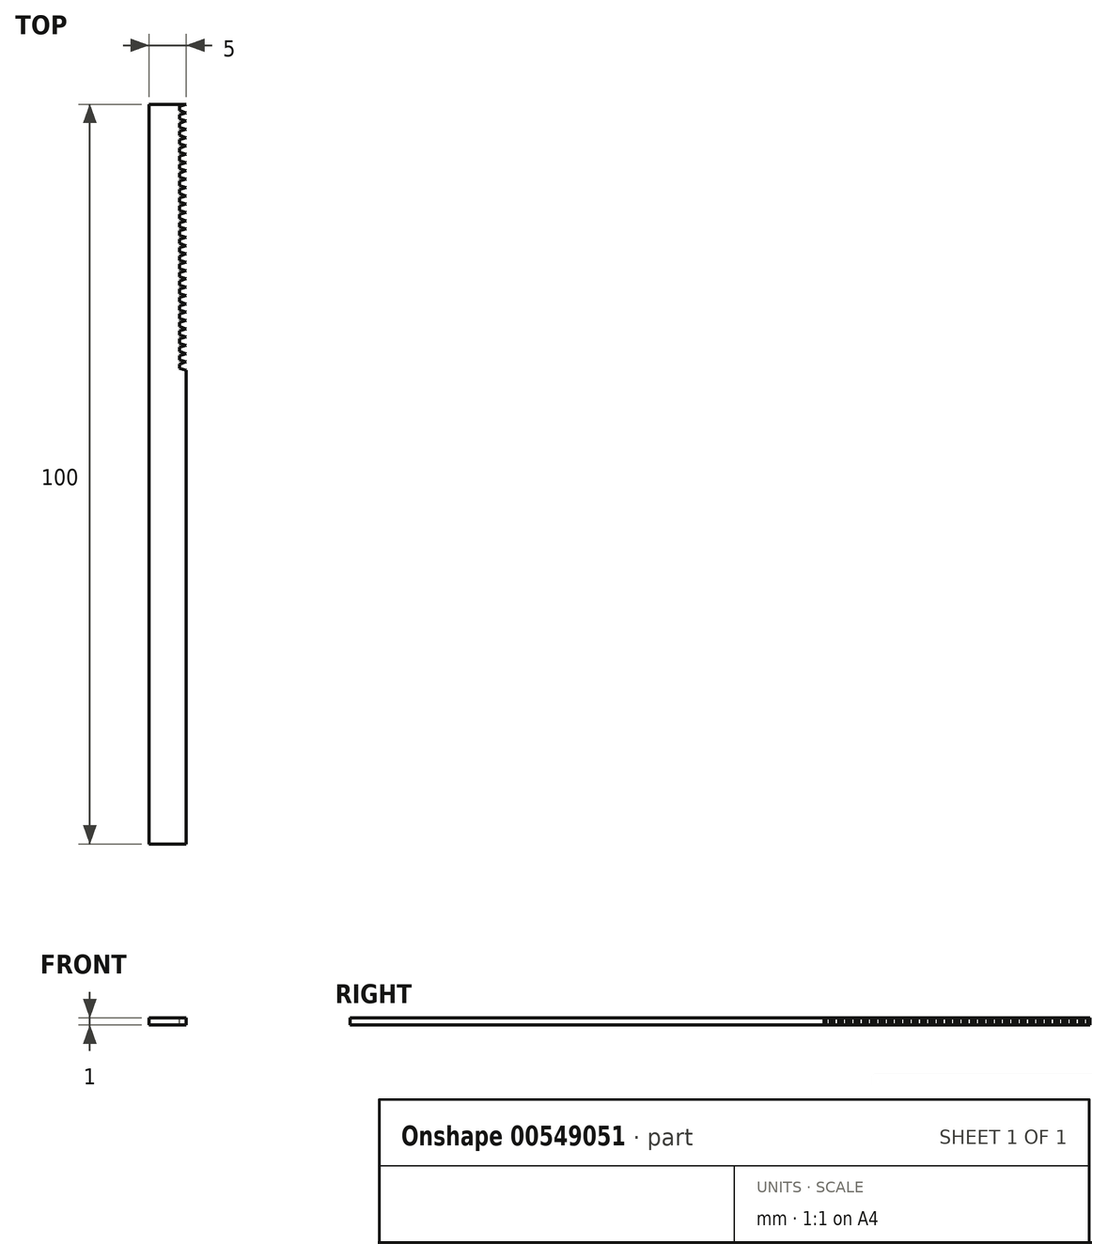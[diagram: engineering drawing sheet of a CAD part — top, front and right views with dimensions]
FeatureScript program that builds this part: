
annotation { "Feature Type Name" : "Feature", "Feature Type Description" : "" }
export const myFeature = defineFeature(function(context is Context, id is Id, definition is map)
    precondition{}
    {
        {
            var Q0;
            Q0=qCreatedBy(makeId("Top.planeOp"),FACE);
            var sketch = newSketch(context, id + "F0", { "sketchPlane" : qUnion([Q0])});
            skLineSegment(sketch, "E0.bottom", {"start": v(-60.96, 22.46) * mm, "end": v(-55.96, 22.46) * mm});
            skLineSegment(sketch, "E0.top", {"start": v(-60.96, -77.54) * mm, "end": v(-55.96, -77.54) * mm});
            skLineSegment(sketch, "E0.left", {"start": v(-60.96, 22.46) * mm, "end": v(-60.96, -77.54) * mm});
            skLineSegment(sketch, "E0.right", {"start": v(-55.96, 22.46) * mm, "end": v(-55.96, -77.54) * mm});
            skSolve(sketch);
        }
        {
            var Q0;
            Q0 = qSketchRegion(id + "F0", true);
            extrude(context, id + "F1", {"entities" : qUnion([Q0]), "endBound" : BoundingType.SYMMETRIC, "depth" : 1 * mm, "offsetDistance" : 25 * mm});
        }
        {
            var Q0;
            Q0=makeQuery(id+"F1.opExtrude","CAP_FACE",FACE,{"disambiguationData":[OSD([sQuery(id+"F0.wireOp",EDGE,"E0.bottom"),sQuery(id+"F0.wireOp",EDGE,"E0.top"),sQuery(id+"F0.wireOp",EDGE,"E0.left"),sQuery(id+"F0.wireOp",EDGE,"E0.right")])],"isStart":false});
            var sketch = newSketch(context, id + "F2", { "sketchPlane" : qUnion([Q0])});
            skLineSegment(sketch, "E1", {"start": v(-56.84, 22.18) * mm, "end": v(-56.84, 21.6) * mm});
            skLineSegment(sketch, "E2", {"start": v(-56.84, 21.6) * mm, "end": v(-55.96, 21.32) * mm});
            skLineSegment(sketch, "E3", {"start": v(-56.84, 22.18) * mm, "end": v(-55.96, 22.45) * mm});
            skLineSegment(sketch, "E4.MirrorCS", {"start": v(-56.84, 21.06) * mm, "end": v(-55.96, 21.32) * mm});
            skLineSegment(sketch, "E5.MirrorCS", {"start": v(-56.84, 20.47) * mm, "end": v(-56.84, 21.06) * mm});
            skLineSegment(sketch, "E6.MirrorCS", {"start": v(-56.84, 20.47) * mm, "end": v(-55.96, 20.2) * mm});
            skLineSegment(sketch, "E7.MirrorCS", {"start": v(-56.84, 19.93) * mm, "end": v(-55.96, 20.2) * mm});
            skLineSegment(sketch, "E8.MirrorCS", {"start": v(-56.84, 19.93) * mm, "end": v(-56.84, 19.34) * mm});
            skLineSegment(sketch, "E9.MirrorCS", {"start": v(-56.84, 19.34) * mm, "end": v(-55.96, 19.08) * mm});
            skLineSegment(sketch, "E10.MirrorCS", {"start": v(-56.84, 18.81) * mm, "end": v(-55.96, 19.08) * mm});
            skLineSegment(sketch, "E11.MirrorCS", {"start": v(-56.84, 18.22) * mm, "end": v(-56.84, 18.81) * mm});
            skLineSegment(sketch, "E12.MirrorCS", {"start": v(-56.84, 18.22) * mm, "end": v(-55.96, 17.95) * mm});
            skLineSegment(sketch, "E13.MirrorCS", {"start": v(-56.84, 14.85) * mm, "end": v(-55.96, 14.58) * mm});
            skLineSegment(sketch, "E14.MirrorCS", {"start": v(-56.84, 13.73) * mm, "end": v(-55.96, 13.46) * mm});
            skLineSegment(sketch, "E15.MirrorCS", {"start": v(-56.84, 15.97) * mm, "end": v(-55.96, 15.7) * mm});
            skLineSegment(sketch, "E16.MirrorCS", {"start": v(-56.84, 14.32) * mm, "end": v(-55.96, 14.58) * mm});
            skLineSegment(sketch, "E17.MirrorCS", {"start": v(-56.84, 13.73) * mm, "end": v(-56.84, 14.32) * mm});
            skLineSegment(sketch, "E18.MirrorCS", {"start": v(-56.84, 17.1) * mm, "end": v(-55.96, 16.83) * mm});
            skLineSegment(sketch, "E19.MirrorCS", {"start": v(-56.84, 15.97) * mm, "end": v(-56.84, 16.56) * mm});
            skLineSegment(sketch, "E20.MirrorCS", {"start": v(-56.84, 15.44) * mm, "end": v(-55.96, 15.7) * mm});
            skLineSegment(sketch, "E21.MirrorCS", {"start": v(-56.84, 17.69) * mm, "end": v(-55.96, 17.95) * mm});
            skLineSegment(sketch, "E22.MirrorCS", {"start": v(-56.84, 16.56) * mm, "end": v(-55.96, 16.83) * mm});
            skLineSegment(sketch, "E23.MirrorCS", {"start": v(-56.84, 15.44) * mm, "end": v(-56.84, 14.85) * mm});
            skLineSegment(sketch, "E24.MirrorCS", {"start": v(-56.84, 17.69) * mm, "end": v(-56.84, 17.1) * mm});
            skLineSegment(sketch, "E25.MirrorCS", {"start": v(-56.84, 9.23) * mm, "end": v(-56.84, 9.82) * mm});
            skLineSegment(sketch, "E26.MirrorCS", {"start": v(-56.84, 5.86) * mm, "end": v(-55.96, 5.6) * mm});
            skLineSegment(sketch, "E27.MirrorCS", {"start": v(-56.84, 4.74) * mm, "end": v(-55.96, 4.47) * mm});
            skLineSegment(sketch, "E28.MirrorCS", {"start": v(-56.84, 5.33) * mm, "end": v(-55.96, 5.6) * mm});
            skLineSegment(sketch, "E29.MirrorCS", {"start": v(-56.84, 4.74) * mm, "end": v(-56.84, 5.33) * mm});
            skLineSegment(sketch, "E30.MirrorCS", {"start": v(-56.84, 12.6) * mm, "end": v(-55.96, 12.34) * mm});
            skLineSegment(sketch, "E31.MirrorCS", {"start": v(-56.84, 10.95) * mm, "end": v(-55.96, 11.21) * mm});
            skLineSegment(sketch, "E32.MirrorCS", {"start": v(-56.84, 13.2) * mm, "end": v(-55.96, 13.46) * mm});
            skLineSegment(sketch, "E33.MirrorCS", {"start": v(-56.84, 11.48) * mm, "end": v(-55.96, 11.21) * mm});
            skLineSegment(sketch, "E34.MirrorCS", {"start": v(-56.84, 9.82) * mm, "end": v(-55.96, 10.1) * mm});
            skLineSegment(sketch, "E35.MirrorCS", {"start": v(-56.84, 10.36) * mm, "end": v(-55.96, 10.1) * mm});
            skLineSegment(sketch, "E36.MirrorCS", {"start": v(-56.84, 6.45) * mm, "end": v(-55.96, 6.72) * mm});
            skLineSegment(sketch, "E37.MirrorCS", {"start": v(-56.84, 7.58) * mm, "end": v(-55.96, 7.84) * mm});
            skLineSegment(sketch, "E38.MirrorCS", {"start": v(-56.84, 6.99) * mm, "end": v(-55.96, 6.72) * mm});
            skLineSegment(sketch, "E39.MirrorCS", {"start": v(-56.84, 8.11) * mm, "end": v(-55.96, 7.84) * mm});
            skLineSegment(sketch, "E40.MirrorCS", {"start": v(-56.84, 10.95) * mm, "end": v(-56.84, 10.36) * mm});
            skLineSegment(sketch, "E41.MirrorCS", {"start": v(-56.84, 12.07) * mm, "end": v(-55.96, 12.34) * mm});
            skLineSegment(sketch, "E42.MirrorCS", {"start": v(-56.84, 8.7) * mm, "end": v(-56.84, 8.11) * mm});
            skLineSegment(sketch, "E43.MirrorCS", {"start": v(-56.84, 8.7) * mm, "end": v(-55.96, 8.97) * mm});
            skLineSegment(sketch, "E44.MirrorCS", {"start": v(-56.84, 6.99) * mm, "end": v(-56.84, 7.58) * mm});
            skLineSegment(sketch, "E45.MirrorCS", {"start": v(-56.84, 9.23) * mm, "end": v(-55.96, 8.97) * mm});
            skLineSegment(sketch, "E46.MirrorCS", {"start": v(-56.84, 6.45) * mm, "end": v(-56.84, 5.86) * mm});
            skLineSegment(sketch, "E47.MirrorCS", {"start": v(-56.84, 11.48) * mm, "end": v(-56.84, 12.07) * mm});
            skLineSegment(sketch, "E48.MirrorCS", {"start": v(-56.84, 13.2) * mm, "end": v(-56.84, 12.6) * mm});
            skLineSegment(sketch, "E49.MirrorCS", {"start": v(-56.84, -11.52) * mm, "end": v(-56.84, -12.1) * mm});
            skLineSegment(sketch, "E50.MirrorCS", {"start": v(-56.84, -9.86) * mm, "end": v(-55.96, -10.13) * mm});
            skLineSegment(sketch, "E51.MirrorCS", {"start": v(-56.84, -10.4) * mm, "end": v(-55.96, -10.13) * mm});
            skLineSegment(sketch, "E52.MirrorCS", {"start": v(-56.84, -10.99) * mm, "end": v(-56.84, -10.4) * mm});
            skLineSegment(sketch, "E53.MirrorCS", {"start": v(-56.84, -11.52) * mm, "end": v(-55.96, -11.25) * mm});
            skLineSegment(sketch, "E54.MirrorCS", {"start": v(-56.84, -10.99) * mm, "end": v(-55.96, -11.25) * mm});
            skLineSegment(sketch, "E55.MirrorCS", {"start": v(-56.84, -12.1) * mm, "end": v(-55.96, -12.38) * mm});
            skLineSegment(sketch, "E56.MirrorCS", {"start": v(-56.84, -13.23) * mm, "end": v(-55.96, -13.5) * mm});
            skLineSegment(sketch, "E57.MirrorCS", {"start": v(-56.84, 2.5) * mm, "end": v(-55.96, 2.23) * mm});
            skLineSegment(sketch, "E58.MirrorCS", {"start": v(-56.84, -6.5) * mm, "end": v(-55.96, -6.76) * mm});
            skLineSegment(sketch, "E59.MirrorCS", {"start": v(-56.84, -9.27) * mm, "end": v(-56.84, -9.86) * mm});
            skLineSegment(sketch, "E60.MirrorCS", {"start": v(-56.84, -12.64) * mm, "end": v(-55.96, -12.38) * mm});
            skLineSegment(sketch, "E61.MirrorCS", {"start": v(-56.84, 4.2) * mm, "end": v(-55.96, 4.47) * mm});
            skLineSegment(sketch, "E62.MirrorCS", {"start": v(-56.84, 0.25) * mm, "end": v(-55.96, -0.02) * mm});
            skLineSegment(sketch, "E63.MirrorCS", {"start": v(-56.84, -13.23) * mm, "end": v(-56.84, -12.64) * mm});
            skLineSegment(sketch, "E64.MirrorCS", {"start": v(-56.84, -5.37) * mm, "end": v(-55.96, -5.64) * mm});
            skLineSegment(sketch, "E65.MirrorCS", {"start": v(-56.84, -0.29) * mm, "end": v(-55.96, -0.02) * mm});
            skLineSegment(sketch, "E66.MirrorCS", {"start": v(-56.84, 4.2) * mm, "end": v(-56.84, 3.62) * mm});
            skLineSegment(sketch, "E67.MirrorCS", {"start": v(-56.84, -3.12) * mm, "end": v(-55.96, -3.39) * mm});
            skLineSegment(sketch, "E68.MirrorCS", {"start": v(-56.84, -0.29) * mm, "end": v(-56.84, -0.88) * mm});
            skLineSegment(sketch, "E69.MirrorCS", {"start": v(-56.84, 1.96) * mm, "end": v(-55.96, 2.23) * mm});
            skLineSegment(sketch, "E70.MirrorCS", {"start": v(-56.84, -2) * mm, "end": v(-55.96, -2.27) * mm});
            skLineSegment(sketch, "E71.MirrorCS", {"start": v(-56.84, -7.62) * mm, "end": v(-55.96, -7.88) * mm});
            skLineSegment(sketch, "E72.MirrorCS", {"start": v(-56.84, -7.03) * mm, "end": v(-56.84, -7.62) * mm});
            skLineSegment(sketch, "E73.MirrorCS", {"start": v(-56.84, -2.53) * mm, "end": v(-56.84, -3.12) * mm});
            skLineSegment(sketch, "E74.MirrorCS", {"start": v(-56.84, -0.88) * mm, "end": v(-55.96, -1.14) * mm});
            skLineSegment(sketch, "E75.MirrorCS", {"start": v(-56.84, -8.15) * mm, "end": v(-55.96, -7.88) * mm});
            skLineSegment(sketch, "E76.MirrorCS", {"start": v(-56.84, 1.96) * mm, "end": v(-56.84, 1.37) * mm});
            skLineSegment(sketch, "E77.MirrorCS", {"start": v(-56.84, 3.62) * mm, "end": v(-55.96, 3.35) * mm});
            skLineSegment(sketch, "E78.MirrorCS", {"start": v(-56.84, -2) * mm, "end": v(-56.84, -1.4) * mm});
            skLineSegment(sketch, "E79.MirrorCS", {"start": v(-56.84, -4.78) * mm, "end": v(-56.84, -5.37) * mm});
            skLineSegment(sketch, "E80.MirrorCS", {"start": v(-56.84, -2.53) * mm, "end": v(-55.96, -2.27) * mm});
            skLineSegment(sketch, "E81.MirrorCS", {"start": v(-56.84, -8.74) * mm, "end": v(-56.84, -8.15) * mm});
            skLineSegment(sketch, "E82.MirrorCS", {"start": v(-56.84, -1.4) * mm, "end": v(-55.96, -1.14) * mm});
            skLineSegment(sketch, "E83.MirrorCS", {"start": v(-56.84, -3.66) * mm, "end": v(-55.96, -3.39) * mm});
            skLineSegment(sketch, "E84.MirrorCS", {"start": v(-56.84, -7.03) * mm, "end": v(-55.96, -6.76) * mm});
            skLineSegment(sketch, "E85.MirrorCS", {"start": v(-56.84, -4.25) * mm, "end": v(-56.84, -3.66) * mm});
            skLineSegment(sketch, "E86.MirrorCS", {"start": v(-56.84, 2.5) * mm, "end": v(-56.84, 3.08) * mm});
            skLineSegment(sketch, "E87.MirrorCS", {"start": v(-56.84, -6.5) * mm, "end": v(-56.84, -5.9) * mm});
            skLineSegment(sketch, "E88.MirrorCS", {"start": v(-56.84, -4.25) * mm, "end": v(-55.96, -4.51) * mm});
            skLineSegment(sketch, "E89.MirrorCS", {"start": v(-56.84, 0.84) * mm, "end": v(-55.96, 1.1) * mm});
            skLineSegment(sketch, "E90.MirrorCS", {"start": v(-56.84, -8.74) * mm, "end": v(-55.96, -9) * mm});
            skLineSegment(sketch, "E91.MirrorCS", {"start": v(-56.84, -5.9) * mm, "end": v(-55.96, -5.64) * mm});
            skLineSegment(sketch, "E92.MirrorCS", {"start": v(-56.84, -4.78) * mm, "end": v(-55.96, -4.51) * mm});
            skLineSegment(sketch, "E93.MirrorCS", {"start": v(-56.84, 3.08) * mm, "end": v(-55.96, 3.35) * mm});
            skLineSegment(sketch, "E94.MirrorCS", {"start": v(-56.84, 0.25) * mm, "end": v(-56.84, 0.84) * mm});
            skLineSegment(sketch, "E95.MirrorCS", {"start": v(-56.84, -9.27) * mm, "end": v(-55.96, -9) * mm});
            skLineSegment(sketch, "E96.MirrorCS", {"start": v(-56.84, 1.37) * mm, "end": v(-55.96, 1.1) * mm});
            skSolve(sketch);
        }
        {
            var Q0;
            Q0=makeQuery(id+"F2.imprint","IMPRINT",FACE,{"disambiguationData":[TD([[makeQuery(id+"F2.imprint","IMPRINT",EDGE,{"derivedFrom":sQuery(id+"F2.wireOp",EDGE,"E1")}),1.0]])]});
            var Q1;
            {var subQ0=sQuery(id+"F2.wireOp",EDGE,"E4.MirrorCS");Q1=makeQuery(id+"F2.imprint","IMPRINT",FACE,{"disambiguationData":[TD([[makeQuery(id+"F2.imprint","IMPRINT",EDGE,{"derivedFrom":subQ0}),-1.0]])]});}
            var Q2;
            {var subQ0=sQuery(id+"F2.wireOp",EDGE,"E7.MirrorCS");Q2=makeQuery(id+"F2.imprint","IMPRINT",FACE,{"disambiguationData":[TD([[makeQuery(id+"F2.imprint","IMPRINT",EDGE,{"derivedFrom":subQ0}),-1.0]])]});}
            var Q3;
            {var subQ0=sQuery(id+"F2.wireOp",EDGE,"E10.MirrorCS");Q3=makeQuery(id+"F2.imprint","IMPRINT",FACE,{"disambiguationData":[TD([[makeQuery(id+"F2.imprint","IMPRINT",EDGE,{"derivedFrom":subQ0}),-1.0]])]});}
            var Q4;
            {var subQ0=sQuery(id+"F2.wireOp",EDGE,"E18.MirrorCS");Q4=makeQuery(id+"F2.imprint","IMPRINT",FACE,{"disambiguationData":[TD([[makeQuery(id+"F2.imprint","IMPRINT",EDGE,{"derivedFrom":subQ0}),1.0]])]});}
            var Q5;
            {var subQ0=sQuery(id+"F2.wireOp",EDGE,"E15.MirrorCS");Q5=makeQuery(id+"F2.imprint","IMPRINT",FACE,{"disambiguationData":[TD([[makeQuery(id+"F2.imprint","IMPRINT",EDGE,{"derivedFrom":subQ0}),1.0]])]});}
            var Q6;
            {var subQ0=sQuery(id+"F2.wireOp",EDGE,"E13.MirrorCS");Q6=makeQuery(id+"F2.imprint","IMPRINT",FACE,{"disambiguationData":[TD([[makeQuery(id+"F2.imprint","IMPRINT",EDGE,{"derivedFrom":subQ0}),1.0]])]});}
            var Q7;
            {var subQ0=sQuery(id+"F2.wireOp",EDGE,"E14.MirrorCS");Q7=makeQuery(id+"F2.imprint","IMPRINT",FACE,{"disambiguationData":[TD([[makeQuery(id+"F2.imprint","IMPRINT",EDGE,{"derivedFrom":subQ0}),1.0]])]});}
            var Q8;
            {var subQ0=sQuery(id+"F2.wireOp",EDGE,"E30.MirrorCS");Q8=makeQuery(id+"F2.imprint","IMPRINT",FACE,{"disambiguationData":[TD([[makeQuery(id+"F2.imprint","IMPRINT",EDGE,{"derivedFrom":subQ0}),1.0]])]});}
            var Q9;
            {var subQ0=sQuery(id+"F2.wireOp",EDGE,"E33.MirrorCS");Q9=makeQuery(id+"F2.imprint","IMPRINT",FACE,{"disambiguationData":[TD([[makeQuery(id+"F2.imprint","IMPRINT",EDGE,{"derivedFrom":subQ0}),1.0]])]});}
            var Q10;
            {var subQ0=sQuery(id+"F2.wireOp",EDGE,"E31.MirrorCS");Q10=makeQuery(id+"F2.imprint","IMPRINT",FACE,{"disambiguationData":[TD([[makeQuery(id+"F2.imprint","IMPRINT",EDGE,{"derivedFrom":subQ0}),-1.0]])]});}
            var Q11;
            Q11=makeQuery(id+"F2.imprint","IMPRINT",FACE,{"disambiguationData":[TD([[makeQuery(id+"F2.imprint","IMPRINT",EDGE,{"derivedFrom":sQuery(id+"F2.wireOp",EDGE,"E25.MirrorCS")}),-1.0]])]});
            var Q12;
            {var subQ0=sQuery(id+"F2.wireOp",EDGE,"E39.MirrorCS");Q12=makeQuery(id+"F2.imprint","IMPRINT",FACE,{"disambiguationData":[TD([[makeQuery(id+"F2.imprint","IMPRINT",EDGE,{"derivedFrom":subQ0}),1.0]])]});}
            var Q13;
            {var subQ0=sQuery(id+"F2.wireOp",EDGE,"E37.MirrorCS");Q13=makeQuery(id+"F2.imprint","IMPRINT",FACE,{"disambiguationData":[TD([[makeQuery(id+"F2.imprint","IMPRINT",EDGE,{"derivedFrom":subQ0}),-1.0]])]});}
            var Q14;
            {var subQ0=sQuery(id+"F2.wireOp",EDGE,"E26.MirrorCS");Q14=makeQuery(id+"F2.imprint","IMPRINT",FACE,{"disambiguationData":[TD([[makeQuery(id+"F2.imprint","IMPRINT",EDGE,{"derivedFrom":subQ0}),1.0]])]});}
            var Q15;
            {var subQ0=sQuery(id+"F2.wireOp",EDGE,"E27.MirrorCS");Q15=makeQuery(id+"F2.imprint","IMPRINT",FACE,{"disambiguationData":[TD([[makeQuery(id+"F2.imprint","IMPRINT",EDGE,{"derivedFrom":subQ0}),1.0]])]});}
            var Q16;
            {var subQ0=sQuery(id+"F2.wireOp",EDGE,"E61.MirrorCS");Q16=makeQuery(id+"F2.imprint","IMPRINT",FACE,{"disambiguationData":[TD([[makeQuery(id+"F2.imprint","IMPRINT",EDGE,{"derivedFrom":subQ0}),-1.0]])]});}
            var Q17;
            {var subQ0=sQuery(id+"F2.wireOp",EDGE,"E57.MirrorCS");Q17=makeQuery(id+"F2.imprint","IMPRINT",FACE,{"disambiguationData":[TD([[makeQuery(id+"F2.imprint","IMPRINT",EDGE,{"derivedFrom":subQ0}),1.0]])]});}
            var Q18;
            {var subQ0=sQuery(id+"F2.wireOp",EDGE,"E69.MirrorCS");Q18=makeQuery(id+"F2.imprint","IMPRINT",FACE,{"disambiguationData":[TD([[makeQuery(id+"F2.imprint","IMPRINT",EDGE,{"derivedFrom":subQ0}),-1.0]])]});}
            var Q19;
            {var subQ0=sQuery(id+"F2.wireOp",EDGE,"E62.MirrorCS");Q19=makeQuery(id+"F2.imprint","IMPRINT",FACE,{"disambiguationData":[TD([[makeQuery(id+"F2.imprint","IMPRINT",EDGE,{"derivedFrom":subQ0}),1.0]])]});}
            var Q20;
            {var subQ0=sQuery(id+"F2.wireOp",EDGE,"E65.MirrorCS");Q20=makeQuery(id+"F2.imprint","IMPRINT",FACE,{"disambiguationData":[TD([[makeQuery(id+"F2.imprint","IMPRINT",EDGE,{"derivedFrom":subQ0}),-1.0]])]});}
            var Q21;
            {var subQ0=sQuery(id+"F2.wireOp",EDGE,"E70.MirrorCS");Q21=makeQuery(id+"F2.imprint","IMPRINT",FACE,{"disambiguationData":[TD([[makeQuery(id+"F2.imprint","IMPRINT",EDGE,{"derivedFrom":subQ0}),1.0]])]});}
            var Q22;
            {var subQ0=sQuery(id+"F2.wireOp",EDGE,"E67.MirrorCS");Q22=makeQuery(id+"F2.imprint","IMPRINT",FACE,{"disambiguationData":[TD([[makeQuery(id+"F2.imprint","IMPRINT",EDGE,{"derivedFrom":subQ0}),1.0]])]});}
            var Q23;
            {var subQ0=sQuery(id+"F2.wireOp",EDGE,"E83.MirrorCS");Q23=makeQuery(id+"F2.imprint","IMPRINT",FACE,{"disambiguationData":[TD([[makeQuery(id+"F2.imprint","IMPRINT",EDGE,{"derivedFrom":subQ0}),-1.0]])]});}
            var Q24;
            {var subQ0=sQuery(id+"F2.wireOp",EDGE,"E64.MirrorCS");Q24=makeQuery(id+"F2.imprint","IMPRINT",FACE,{"disambiguationData":[TD([[makeQuery(id+"F2.imprint","IMPRINT",EDGE,{"derivedFrom":subQ0}),1.0]])]});}
            var Q25;
            {var subQ0=sQuery(id+"F2.wireOp",EDGE,"E58.MirrorCS");Q25=makeQuery(id+"F2.imprint","IMPRINT",FACE,{"disambiguationData":[TD([[makeQuery(id+"F2.imprint","IMPRINT",EDGE,{"derivedFrom":subQ0}),1.0]])]});}
            var Q26;
            {var subQ0=sQuery(id+"F2.wireOp",EDGE,"E71.MirrorCS");Q26=makeQuery(id+"F2.imprint","IMPRINT",FACE,{"disambiguationData":[TD([[makeQuery(id+"F2.imprint","IMPRINT",EDGE,{"derivedFrom":subQ0}),1.0]])]});}
            var Q27;
            {var subQ0=sQuery(id+"F2.wireOp",EDGE,"E75.MirrorCS");Q27=makeQuery(id+"F2.imprint","IMPRINT",FACE,{"disambiguationData":[TD([[makeQuery(id+"F2.imprint","IMPRINT",EDGE,{"derivedFrom":subQ0}),-1.0]])]});}
            var Q28;
            {var subQ0=sQuery(id+"F2.wireOp",EDGE,"E50.MirrorCS");Q28=makeQuery(id+"F2.imprint","IMPRINT",FACE,{"disambiguationData":[TD([[makeQuery(id+"F2.imprint","IMPRINT",EDGE,{"derivedFrom":subQ0}),1.0]])]});}
            var Q29;
            {var subQ0=sQuery(id+"F2.wireOp",EDGE,"E51.MirrorCS");Q29=makeQuery(id+"F2.imprint","IMPRINT",FACE,{"disambiguationData":[TD([[makeQuery(id+"F2.imprint","IMPRINT",EDGE,{"derivedFrom":subQ0}),-1.0]])]});}
            var Q30;
            Q30=makeQuery(id+"F2.imprint","IMPRINT",FACE,{"disambiguationData":[TD([[makeQuery(id+"F2.imprint","IMPRINT",EDGE,{"derivedFrom":sQuery(id+"F2.wireOp",EDGE,"E49.MirrorCS")}),1.0]])]});
            var Q31;
            {var subQ0=sQuery(id+"F2.wireOp",EDGE,"E56.MirrorCS");Q31=makeQuery(id+"F2.imprint","IMPRINT",FACE,{"disambiguationData":[TD([[makeQuery(id+"F2.imprint","IMPRINT",EDGE,{"derivedFrom":subQ0}),1.0]])]});}
            extrude(context, id + "F3", {"entities" : qUnion([Q0, Q1, Q2, Q3, Q4, Q5, Q6, Q7, Q8, Q9, Q10, Q11, Q12, Q13, Q14, Q15, Q16, Q17, Q18, Q19, Q20, Q21, Q22, Q23, Q24, Q25, Q26, Q27, Q28, Q29, Q30, Q31]), "operationType" : NewBodyOperationType.REMOVE, "oppositeDirection" : true, "depth" : 25 * mm, "offsetDistance" : 25 * mm});
        }
    });
